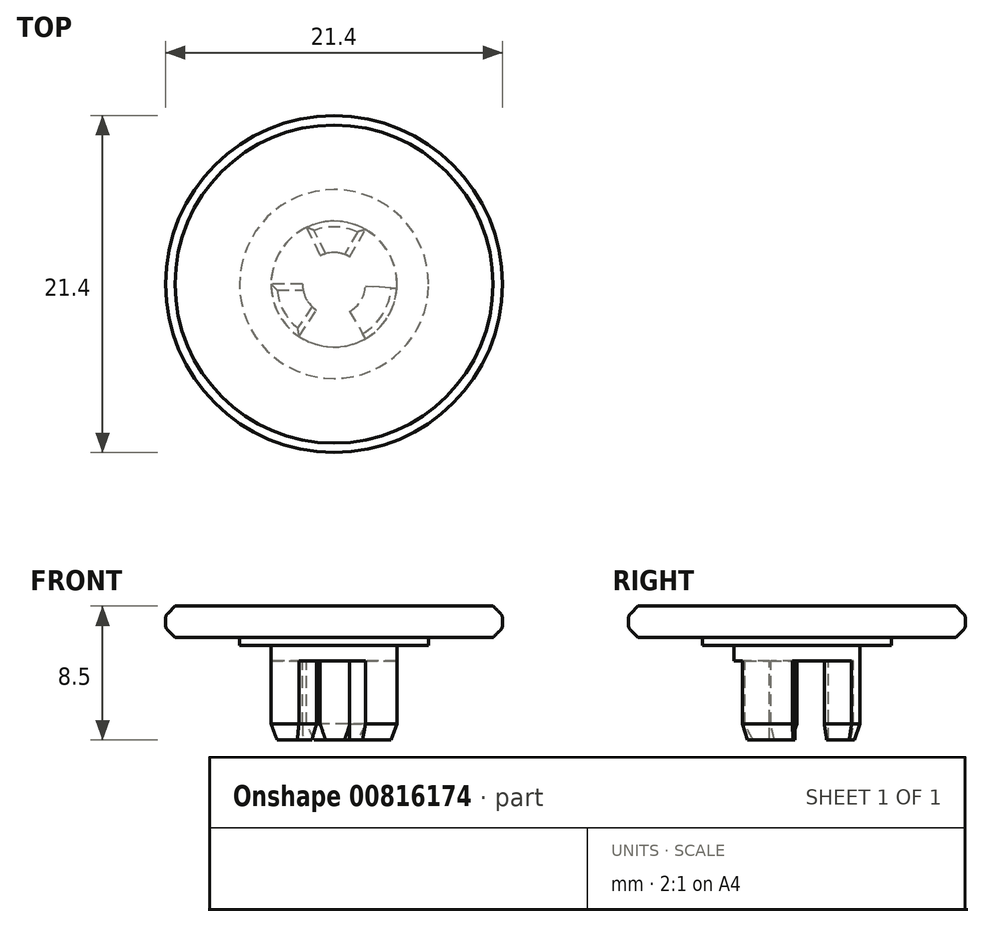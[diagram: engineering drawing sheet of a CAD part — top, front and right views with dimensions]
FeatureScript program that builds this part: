
annotation { "Feature Type Name" : "Feature", "Feature Type Description" : "" }
export const myFeature = defineFeature(function(context is Context, id is Id, definition is map)
    precondition{}
    {
        {
            var Q0;
            Q0=qCreatedBy(makeId("Front.planeOp"),FACE);
            var sketch = newSketch(context, id + "F0", { "sketchPlane" : qUnion([Q0])});
            skLineSegment(sketch, "E0", {"start": v(0, 8.5) * mm, "end": v(10.7, 8.5) * mm});
            skLineSegment(sketch, "E1", {"start": v(10.7, 8.5) * mm, "end": v(10.7, 6.5) * mm});
            skLineSegment(sketch, "E2", {"start": v(4, 6) * mm, "end": v(4, 0) * mm});
            skLineSegment(sketch, "E3", {"start": v(4, 6) * mm, "end": v(6, 6) * mm});
            skLineSegment(sketch, "E4", {"start": v(6, 6) * mm, "end": v(6, 6.5) * mm});
            skLineSegment(sketch, "E5", {"start": v(6, 6.5) * mm, "end": v(10.7, 6.5) * mm});
            skLineSegment(sketch, "E6", {"start": v(0, 8.5) * mm, "end": v(0, 5) * mm});
            skLineSegment(sketch, "E7", {"start": v(0, 5) * mm, "end": v(2, 5) * mm});
            skLineSegment(sketch, "E8", {"start": v(2, 5) * mm, "end": v(2, 0) * mm});
            skLineSegment(sketch, "E9", {"start": v(2, 0) * mm, "end": v(4, 0) * mm});
            skSolve(sketch);
        }
        {
            var Q0;
            Q0=makeQuery(id+"F0.imprint","IMPRINT",FACE,{"disambiguationData":[TD([[makeQuery(id+"F0.imprint","IMPRINT",EDGE,{"derivedFrom":sQuery(id+"F0.wireOp",EDGE,"E0")}),-1.0]])]});
            var Q1;
            Q1=sQuery(id+"F0.wireOp",EDGE,"E6");
            revolve(context, id + "F1", {"surfaceOperationType" : NewSurfaceOperationType.NEW, "entities" : qUnion([Q0]), "axis" : qUnion([Q1]), "revolveType" : RevolveType.FULL});
        }
        {
            var Q0;
            Q0=makeQuery(id+"F1.opRevolve","SWEPT_FACE",FACE,{"disambiguationData":[OSD([sQuery(id+"F0.wireOp",EDGE,"E9")])]});
            var sketch = newSketch(context, id + "F2", { "sketchPlane" : qUnion([Q0])});
            skLineSegment(sketch, "E10", {"start": v(0, 0) * mm, "end": v(-6, 0) * mm});
            skLineSegment(sketch, "E11", {"start": v(-6, 0) * mm, "end": v(-2.63, -5.4) * mm});
            skLineSegment(sketch, "E12", {"start": v(-2.63, -5.4) * mm, "end": v(0, 0) * mm});
            skLineSegment(sketch, "E13.1.0", {"start": v(0, 0) * mm, "end": v(3, -5.2) * mm});
            skLineSegment(sketch, "E13.1.1", {"start": v(5.99, 0.42) * mm, "end": v(0, 0) * mm});
            skLineSegment(sketch, "E13.1.2", {"start": v(3, -5.2) * mm, "end": v(5.99, 0.42) * mm});
            skLineSegment(sketch, "E13.2.0", {"start": v(0, 0) * mm, "end": v(3, 5.2) * mm});
            skLineSegment(sketch, "E13.2.1", {"start": v(-3.36, 4.97) * mm, "end": v(0, 0) * mm});
            skLineSegment(sketch, "E13.2.2", {"start": v(3, 5.2) * mm, "end": v(-3.36, 4.97) * mm});
            skPoint(sketch, "E13.center", {"position": v(0, 0) * mm});
            skCircle(sketch, "E14", {"center": v(0, 0) * mm, "radius": 1.14 * mm});
            skSolve(sketch);
        }
        {
            var Q0;
            {var subQ0=sQuery(id+"F2.wireOp",EDGE,"E13.1.2");Q0=makeQuery(id+"F2.imprint","IMPRINT",FACE,{"disambiguationData":[TD([[makeQuery(id+"F2.imprint","IMPRINT",EDGE,{"derivedFrom":subQ0}),1.0]])]});}
            var Q1;
            {var subQ0=sQuery(id+"F2.wireOp",EDGE,"E13.2.2");Q1=makeQuery(id+"F2.imprint","IMPRINT",FACE,{"disambiguationData":[TD([[makeQuery(id+"F2.imprint","IMPRINT",EDGE,{"derivedFrom":subQ0}),1.0]])]});}
            var Q2;
            {var subQ0=sQuery(id+"F2.wireOp",EDGE,"E10");var subQ1=sQuery(id+"F0.wireOp",EDGE,"E9");var subQ2=makeQuery(id+"F1.opRevolve","SWEPT_EDGE",EDGE,{"disambiguationData":[OSD([sQuery(id+"F0.wireOp",EDGE,"E2"),subQ1])]});var subQ3=makeQuery(id+"F2.imprint","INTERSECT",VERTEX,{"derivedFrom":[subQ2,subQ0]});Q2=makeQuery(id+"F2.imprint","IMPRINT",FACE,{"disambiguationData":[TD([[makeQuery(id+"F2.imprint","IMPRINT",EDGE,{"disambiguationData":[TD([[subQ3,1.0]])],"derivedFrom":subQ0}),1.0]])]});}
            var Q3;
            {var subQ0=sQuery(id+"F2.wireOp",EDGE,"E11");Q3=makeQuery(id+"F2.imprint","IMPRINT",FACE,{"disambiguationData":[TD([[makeQuery(id+"F2.imprint","IMPRINT",EDGE,{"derivedFrom":subQ0}),1.0]])]});}
            var Q4;
            {var subQ0=sQuery(id+"F2.wireOp",EDGE,"E13.1.0");var subQ1=sQuery(id+"F0.wireOp",EDGE,"E9");var subQ2=makeQuery(id+"F1.opRevolve","SWEPT_EDGE",EDGE,{"disambiguationData":[OSD([sQuery(id+"F0.wireOp",EDGE,"E2"),subQ1])]});var subQ3=makeQuery(id+"F2.imprint","INTERSECT",VERTEX,{"derivedFrom":[subQ2,subQ0]});Q4=makeQuery(id+"F2.imprint","IMPRINT",FACE,{"disambiguationData":[TD([[makeQuery(id+"F2.imprint","IMPRINT",EDGE,{"disambiguationData":[TD([[subQ3,1.0]])],"derivedFrom":subQ0}),1.0]])]});}
            var Q5;
            {var subQ0=sQuery(id+"F2.wireOp",EDGE,"E13.2.0");var subQ1=sQuery(id+"F0.wireOp",EDGE,"E9");var subQ2=makeQuery(id+"F1.opRevolve","SWEPT_EDGE",EDGE,{"disambiguationData":[OSD([sQuery(id+"F0.wireOp",EDGE,"E2"),subQ1])]});var subQ3=makeQuery(id+"F2.imprint","INTERSECT",VERTEX,{"derivedFrom":[subQ2,subQ0]});Q5=makeQuery(id+"F2.imprint","IMPRINT",FACE,{"disambiguationData":[TD([[makeQuery(id+"F2.imprint","IMPRINT",EDGE,{"disambiguationData":[TD([[subQ3,1.0]])],"derivedFrom":subQ0}),1.0]])]});}
            var Q6;
            {var subQ0=sQuery(id+"F2.wireOp",EDGE,"E14");var subQ1=sQuery(id+"F2.wireOp",EDGE,"E10");var subQ2=makeQuery(id+"F2.imprint","INTERSECT",VERTEX,{"derivedFrom":[subQ1,subQ0]});Q6=makeQuery(id+"F2.imprint","IMPRINT",FACE,{"disambiguationData":[TD([[makeQuery(id+"F2.imprint","IMPRINT",EDGE,{"disambiguationData":[TD([[subQ2,-1.0]])],"derivedFrom":subQ0}),-1.0]])]});}
            var Q7;
            {var subQ1=sQuery(id+"F2.wireOp",EDGE,"E10");var subQ3=sQuery(id+"F2.wireOp",EDGE,"E14");var subQ4=makeQuery(id+"F2.imprint","INTERSECT",VERTEX,{"derivedFrom":[subQ1,subQ3]});Q7=makeQuery(id+"F2.imprint","IMPRINT",FACE,{"disambiguationData":[TD([[makeQuery(id+"F2.imprint","IMPRINT",EDGE,{"disambiguationData":[TD([[subQ4,-1.0]])],"derivedFrom":subQ3}),1.0]])]});}
            var Q8;
            {var subQ1=sQuery(id+"F2.wireOp",EDGE,"E13.2.0");var subQ3=sQuery(id+"F2.wireOp",EDGE,"E14");var subQ4=makeQuery(id+"F2.imprint","INTERSECT",VERTEX,{"derivedFrom":[subQ1,subQ3]});Q8=makeQuery(id+"F2.imprint","IMPRINT",FACE,{"disambiguationData":[TD([[makeQuery(id+"F2.imprint","IMPRINT",EDGE,{"disambiguationData":[TD([[subQ4,-1.0]])],"derivedFrom":subQ3}),1.0]])]});}
            var Q9;
            {var subQ0=sQuery(id+"F2.wireOp",EDGE,"E14");var subQ1=sQuery(id+"F2.wireOp",EDGE,"E13.2.0");var subQ2=makeQuery(id+"F2.imprint","INTERSECT",VERTEX,{"derivedFrom":[subQ1,subQ0]});Q9=makeQuery(id+"F2.imprint","IMPRINT",FACE,{"disambiguationData":[TD([[makeQuery(id+"F2.imprint","IMPRINT",EDGE,{"disambiguationData":[TD([[subQ2,-1.0]])],"derivedFrom":subQ0}),-1.0]])]});}
            var Q10;
            {var subQ1=sQuery(id+"F2.wireOp",EDGE,"E13.1.0");var subQ3=sQuery(id+"F2.wireOp",EDGE,"E14");var subQ4=makeQuery(id+"F2.imprint","INTERSECT",VERTEX,{"derivedFrom":[subQ1,subQ3]});Q10=makeQuery(id+"F2.imprint","IMPRINT",FACE,{"disambiguationData":[TD([[makeQuery(id+"F2.imprint","IMPRINT",EDGE,{"disambiguationData":[TD([[subQ4,-1.0]])],"derivedFrom":subQ3}),1.0]])]});}
            var Q11;
            {var subQ0=sQuery(id+"F2.wireOp",EDGE,"E14");var subQ1=sQuery(id+"F2.wireOp",EDGE,"E13.1.0");var subQ2=makeQuery(id+"F2.imprint","INTERSECT",VERTEX,{"derivedFrom":[subQ1,subQ0]});Q11=makeQuery(id+"F2.imprint","IMPRINT",FACE,{"disambiguationData":[TD([[makeQuery(id+"F2.imprint","IMPRINT",EDGE,{"disambiguationData":[TD([[subQ2,-1.0]])],"derivedFrom":subQ0}),-1.0]])]});}
            extrude(context, id + "F3", {"entities" : qUnion([Q0, Q1, Q2, Q3, Q4, Q5, Q6, Q7, Q8, Q9, Q10, Q11]), "operationType" : NewBodyOperationType.REMOVE, "oppositeDirection" : true, "depth" : 5 * mm, "offsetDistance" : 25 * mm});
        }
        {
            var Q0;
            {var subQ0=sQuery(id+"F0.wireOp",EDGE,"E2");var subQ1=sQuery(id+"F0.wireOp",EDGE,"E9");Q0=makeQuery(id+"F3.boolean.opBoolean","SPLIT",EDGE,{"disambiguationData":[TD([makeQuery(id+"F3.opExtrude","SWEPT_FACE",FACE,{"disambiguationData":[OSD([sQuery(id+"F2.wireOp",EDGE,"E10")])]})])],"derivedFrom":makeQuery(id+"F1.opRevolve","SWEPT_EDGE",EDGE,{"disambiguationData":[OSD([subQ0,subQ1])]})});}
            var Q1;
            {var subQ0=sQuery(id+"F0.wireOp",EDGE,"E2");var subQ1=sQuery(id+"F0.wireOp",EDGE,"E9");Q1=makeQuery(id+"F3.boolean.opBoolean","SPLIT",EDGE,{"disambiguationData":[TD([makeQuery(id+"F3.opExtrude","SWEPT_FACE",FACE,{"disambiguationData":[OSD([sQuery(id+"F2.wireOp",EDGE,"E12")])]})])],"derivedFrom":makeQuery(id+"F1.opRevolve","SWEPT_EDGE",EDGE,{"disambiguationData":[OSD([subQ0,subQ1])]})});}
            var Q2;
            Q2=makeQuery(id+"F3.boolean.opBoolean","COPY",EDGE,{"derivedFrom":makeQuery(id+"F3.opExtrude","CAP_EDGE",EDGE,{"disambiguationData":[OSD([sQuery(id+"F2.wireOp",EDGE,"E10")])],"isStart":true})});
            var Q3;
            Q3=makeQuery(id+"F3.boolean.opBoolean","COPY",EDGE,{"derivedFrom":makeQuery(id+"F3.opExtrude","CAP_EDGE",EDGE,{"disambiguationData":[OSD([sQuery(id+"F2.wireOp",EDGE,"E13.2.1")])],"isStart":true})});
            var Q4;
            Q4=makeQuery(id+"F3.boolean.opBoolean","COPY",EDGE,{"derivedFrom":makeQuery(id+"F3.opExtrude","CAP_EDGE",EDGE,{"disambiguationData":[OSD([sQuery(id+"F2.wireOp",EDGE,"E13.2.0")])],"isStart":true})});
            var Q5;
            {var subQ0=sQuery(id+"F0.wireOp",EDGE,"E2");var subQ1=sQuery(id+"F0.wireOp",EDGE,"E9");Q5=makeQuery(id+"F3.boolean.opBoolean","SPLIT",EDGE,{"disambiguationData":[TD([makeQuery(id+"F3.opExtrude","SWEPT_FACE",FACE,{"disambiguationData":[OSD([sQuery(id+"F2.wireOp",EDGE,"E13.1.1")])]})])],"derivedFrom":makeQuery(id+"F1.opRevolve","SWEPT_EDGE",EDGE,{"disambiguationData":[OSD([subQ0,subQ1])]})});}
            var Q6;
            Q6=makeQuery(id+"F3.boolean.opBoolean","COPY",EDGE,{"derivedFrom":makeQuery(id+"F3.opExtrude","CAP_EDGE",EDGE,{"disambiguationData":[OSD([sQuery(id+"F2.wireOp",EDGE,"E13.1.1")])],"isStart":true})});
            var Q7;
            Q7=makeQuery(id+"F3.boolean.opBoolean","COPY",EDGE,{"derivedFrom":makeQuery(id+"F3.opExtrude","CAP_EDGE",EDGE,{"disambiguationData":[OSD([sQuery(id+"F2.wireOp",EDGE,"E12")])],"isStart":true})});
            var Q8;
            Q8=makeQuery(id+"F3.boolean.opBoolean","COPY",EDGE,{"derivedFrom":makeQuery(id+"F3.opExtrude","CAP_EDGE",EDGE,{"disambiguationData":[OSD([sQuery(id+"F2.wireOp",EDGE,"E13.1.0")])],"isStart":true})});
            chamfer(context, id + "F4", {"entities" : qUnion([Q0, Q1, Q2, Q3, Q4, Q5, Q6, Q7, Q8]), "chamferType" : ChamferType.OFFSET_ANGLE, "width" : 1 * mm, "oppositeDirection" : false, "angle" : 20 * degree, "tangentPropagation" : true});
        }
        {
            var Q0;
            Q0=makeQuery(id+"F1.opRevolve","SWEPT_EDGE",EDGE,{"disambiguationData":[OSD([sQuery(id+"F0.wireOp",EDGE,"E0"),sQuery(id+"F0.wireOp",EDGE,"E1")])]});
            var Q1;
            Q1=makeQuery(id+"F1.opRevolve","SWEPT_EDGE",EDGE,{"disambiguationData":[OSD([sQuery(id+"F0.wireOp",EDGE,"E1"),sQuery(id+"F0.wireOp",EDGE,"E5")])]});
            chamfer(context, id + "F5", {"entities" : qUnion([Q0, Q1]), "width" : 0.6 * mm, "tangentPropagation" : true});
        }
        {
            var Q0;
            Q0=makeQuery(id+"F1.opRevolve","SWEPT_FACE",FACE,{"disambiguationData":[OSD([sQuery(id+"F0.wireOp",EDGE,"E1")])]});
            fillet(context, id + "F6", {"entities" : qUnion([Q0]), "radius" : 0.5 * mm, "tangentPropagation" : true, "allowEdgeOverflow" : false});
        }
    });
